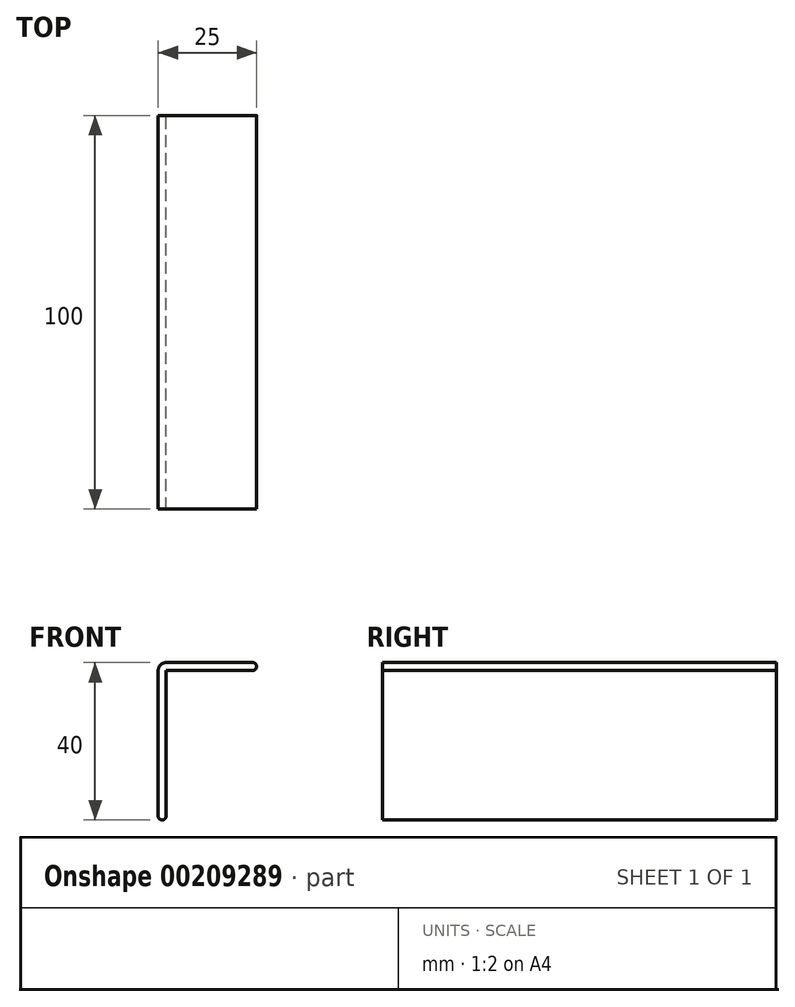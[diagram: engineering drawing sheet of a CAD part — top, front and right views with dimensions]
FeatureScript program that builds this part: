
annotation { "Feature Type Name" : "Feature", "Feature Type Description" : "" }
export const myFeature = defineFeature(function(context is Context, id is Id, definition is map)
    precondition{}
    {
        {
            var Q0;
            Q0=qCreatedBy(makeId("Front.planeOp"),FACE);
            var sketch = newSketch(context, id + "F0", { "sketchPlane" : qUnion([Q0])});
            skLineSegment(sketch, "E0.bottom", {"start": v(-11.5, -20) * mm, "end": v(-11.5, -20) * mm});
            skLineSegment(sketch, "E0.top", {"start": v(11.5, 20) * mm, "end": v(-10.5, 20) * mm});
            skLineSegment(sketch, "E0.right", {"start": v(-12.5, -19) * mm, "end": v(-12.5, 18) * mm});
            skPoint(sketch, "E0.middle", {"position": v(0, 0) * mm});
            skArc(sketch, "E1.filletArc", {"start": v(-10.5, 20) * mm, "mid": v(-11.91, 19.41) * mm, "end": v(-12.5, 18) * mm});
            skLineSegment(sketch, "E2.3", {"start": v(-10.5, -18) * mm, "end": v(-10.5, 18) * mm});
            skLineSegment(sketch, "E3", {"start": v(-10.5, -12.36) * mm, "end": v(-10.5, -19) * mm});
            skPoint(sketch, "E4.visualSharp", {"position": v(-10.5, -20) * mm});
            skArc(sketch, "E4.filletArc", {"start": v(-11.5, -20) * mm, "mid": v(-10.8, -19.7) * mm, "end": v(-10.5, -19) * mm});
            skPoint(sketch, "E5.visualSharp", {"position": v(-12.5, -20) * mm});
            skArc(sketch, "E5.filletArc", {"start": v(-12.5, -19) * mm, "mid": v(-12.2, -19.7) * mm, "end": v(-11.5, -20) * mm});
            skPoint(sketch, "E6.visualSharp", {"position": v(12.5, 20) * mm});
            skArc(sketch, "E6.filletArc", {"start": v(11.5, 18) * mm, "mid": v(12.5, 19) * mm, "end": v(11.5, 20) * mm});
            skLineSegment(sketch, "E7", {"start": v(11.5, 18) * mm, "end": v(-10.5, 18) * mm});
            skSolve(sketch);
        }
        {
            var Q0;
            Q0=makeQuery(id+"F0.imprint","IMPRINT",FACE,{"disambiguationData":[TD([[makeQuery(id+"F0.imprint","IMPRINT",EDGE,{"derivedFrom":sQuery(id+"F0.wireOp",EDGE,"E0.top")}),1.0]])]});
            extrude(context, id + "F1", {"entities" : qUnion([Q0]), "depth" : 100 * mm});
        }
    });
